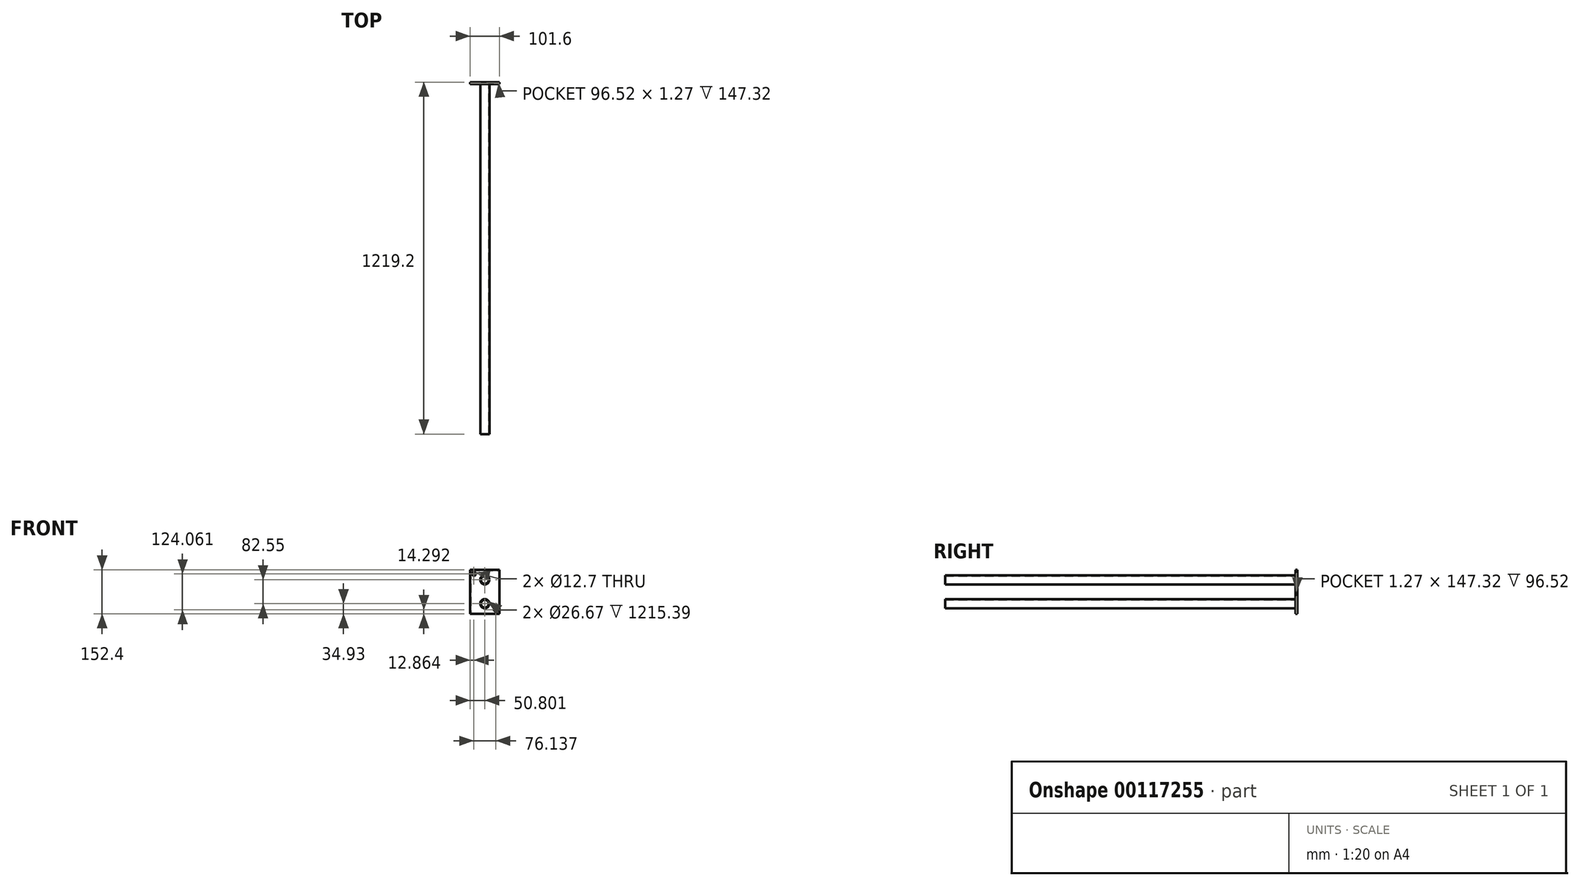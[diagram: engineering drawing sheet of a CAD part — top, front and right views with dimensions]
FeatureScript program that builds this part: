
annotation { "Feature Type Name" : "Feature", "Feature Type Description" : "" }
export const myFeature = defineFeature(function(context is Context, id is Id, definition is map)
    precondition{}
    {
        {
            var Q0;
            Q0=qCreatedBy(makeId("Front.planeOp"),FACE);
            var sketch = newSketch(context, id + "F0", { "sketchPlane" : qUnion([Q0])});
            skLineSegment(sketch, "E0.bottom", {"start": v(-2540.64, 931.55) * mm, "end": v(-2439.04, 931.55) * mm});
            skLineSegment(sketch, "E0.top", {"start": v(-2540.64, 779.15) * mm, "end": v(-2439.04, 779.15) * mm});
            skLineSegment(sketch, "E0.left", {"start": v(-2540.64, 931.55) * mm, "end": v(-2540.64, 779.15) * mm});
            skLineSegment(sketch, "E0.right", {"start": v(-2439.04, 931.55) * mm, "end": v(-2439.04, 779.15) * mm});
            skCircle(sketch, "E1", {"center": v(-2489.84, 896.63) * mm, "radius": 15.88 * mm});
            skCircle(sketch, "E2", {"center": v(-2489.84, 814.08) * mm, "radius": 15.88 * mm});
            skCircle(sketch, "E3", {"center": v(-2527.78, 917.5) * mm, "radius": 6.35 * mm});
            skCircle(sketch, "E4", {"center": v(-2451.64, 793.44) * mm, "radius": 6.35 * mm});
            skSolve(sketch);
        }
        {
            var Q0;
            Q0=makeQuery(id+"F0.imprint","IMPRINT",FACE,{"disambiguationData":[TD([[makeQuery(id+"F0.imprint","IMPRINT",EDGE,{"derivedFrom":sQuery(id+"F0.wireOp",EDGE,"E0.bottom")}),-1.0]])]});
            extrude(context, id + "F1", {"entities" : qUnion([Q0]), "depth" : 6.35 * mm});
        }
        {
            var Q0;
            Q0=makeQuery(id+"F0.imprint","IMPRINT",FACE,{"disambiguationData":[TD([[makeQuery(id+"F0.imprint","IMPRINT",EDGE,{"derivedFrom":sQuery(id+"F0.wireOp",EDGE,"E1")}),1.0]])]});
            var Q1;
            Q1=makeQuery(id+"F0.imprint","IMPRINT",FACE,{"disambiguationData":[TD([[makeQuery(id+"F0.imprint","IMPRINT",EDGE,{"derivedFrom":sQuery(id+"F0.wireOp",EDGE,"E2")}),1.0]])]});
            extrude(context, id + "F2", {"entities" : qUnion([Q0, Q1]), "operationType" : NewBodyOperationType.ADD, "depth" : 1219.2 * mm});
        }
        {
            var Q0;
            Q0=makeQuery(id+"F2.opExtrude","CAP_FACE",FACE,{"disambiguationData":[OSD([sQuery(id+"F0.wireOp",EDGE,"E1")])],"isStart":false});
            var Q1;
            Q1=makeQuery(id+"F2.opExtrude","CAP_FACE",FACE,{"disambiguationData":[OSD([sQuery(id+"F0.wireOp",EDGE,"E2")])],"isStart":false});
            shell(context, id + "F3", {"entities" : qUnion([Q0, Q1]), "thickness" : 2.54 * mm});
        }
    });
